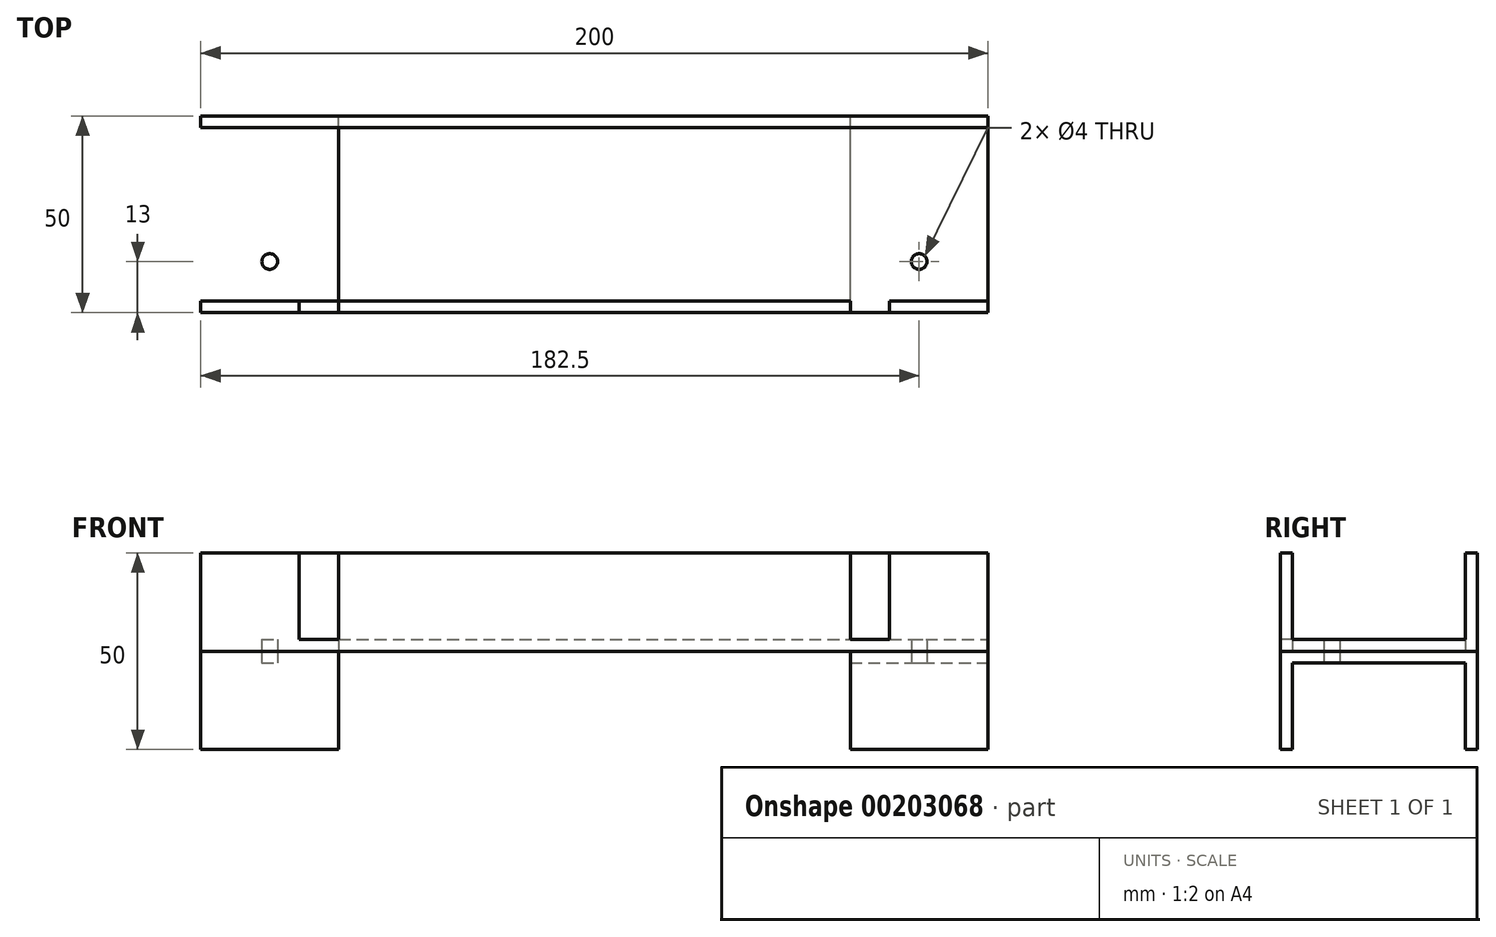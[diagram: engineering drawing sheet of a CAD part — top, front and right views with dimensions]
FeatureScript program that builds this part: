
annotation { "Feature Type Name" : "Feature", "Feature Type Description" : "" }
export const myFeature = defineFeature(function(context is Context, id is Id, definition is map)
    precondition{}
    {
        {
            var Q0;
            Q0=qCreatedBy(makeId("Front.planeOp"),FACE);
            var sketch = newSketch(context, id + "F0", { "sketchPlane" : qUnion([Q0])});
            skLineSegment(sketch, "E0.bottom", {"start": v(100, -12.5) * mm, "end": v(-100, -12.5) * mm});
            skLineSegment(sketch, "E0.top", {"start": v(100, 12.5) * mm, "end": v(-100, 12.5) * mm});
            skLineSegment(sketch, "E0.left", {"start": v(100, -12.5) * mm, "end": v(100, 12.5) * mm});
            skLineSegment(sketch, "E0.right", {"start": v(-100, -12.5) * mm, "end": v(-100, 12.5) * mm});
            skPoint(sketch, "E0.middle", {"position": v(0, 0) * mm});
            skSolve(sketch);
        }
        {
            var Q0;
            Q0 = qSketchRegion(id + "F0", true);
            extrude(context, id + "F1", {"entities" : qUnion([Q0]), "depth" : 50 * mm});
        }
        {
            var Q0;
            Q0=makeQuery(id+"F1.opExtrude","SWEPT_FACE",FACE,{"disambiguationData":[OSD([sQuery(id+"F0.wireOp",EDGE,"E0.left")])]});
            var sketch = newSketch(context, id + "F2", { "sketchPlane" : qUnion([Q0])});
            skLineSegment(sketch, "E1.bottom", {"start": v(-47, 12.5) * mm, "end": v(-3, 12.5) * mm});
            skLineSegment(sketch, "E1.top", {"start": v(-47, -9.5) * mm, "end": v(-3, -9.5) * mm});
            skLineSegment(sketch, "E1.left", {"start": v(-47, 12.5) * mm, "end": v(-47, -9.5) * mm});
            skLineSegment(sketch, "E1.right", {"start": v(-3, 12.5) * mm, "end": v(-3, -9.5) * mm});
            skLineSegment(sketch, "E2", {"start": v(-47, 4.4) * mm, "end": v(-50, 4.4) * mm});
            skLineSegment(sketch, "E3", {"start": v(-23.42, -9.5) * mm, "end": v(-23.42, -12.5) * mm});
            skLineSegment(sketch, "E4", {"start": v(-3, 6.89) * mm, "end": v(0, 6.89) * mm});
            skSolve(sketch);
        }
        {
            var Q0;
            {var subQ1=sQuery(id+"F2.wireOp",EDGE,"E1.bottom");Q0=makeQuery(id+"F2.imprint","IMPRINT",FACE,{"disambiguationData":[TD([[makeQuery(id+"F2.imprint","IMPRINT",EDGE,{"derivedFrom":subQ1}),-1.0]])]});}
            extrude(context, id + "F3", {"entities" : qUnion([Q0]), "operationType" : NewBodyOperationType.REMOVE, "endBound" : BoundingType.THROUGH_ALL, "oppositeDirection" : true, "depth" : 25 * mm});
        }
        {
            var Q0;
            Q0=makeQuery(id+"F1.opExtrude","CAP_FACE",FACE,{"disambiguationData":[OSD([sQuery(id+"F0.wireOp",EDGE,"E0.bottom"),sQuery(id+"F0.wireOp",EDGE,"E0.top"),sQuery(id+"F0.wireOp",EDGE,"E0.left"),sQuery(id+"F0.wireOp",EDGE,"E0.right")])],"isStart":false});
            var sketch = newSketch(context, id + "F4", { "sketchPlane" : qUnion([Q0])});
            skLineSegment(sketch, "E5.bottom", {"start": v(-75, 12.5) * mm, "end": v(-65, 12.5) * mm});
            skLineSegment(sketch, "E5.top", {"start": v(-75, -9.5) * mm, "end": v(-65, -9.5) * mm});
            skLineSegment(sketch, "E5.left", {"start": v(-75, 12.5) * mm, "end": v(-75, -9.5) * mm});
            skLineSegment(sketch, "E5.right", {"start": v(-65, 12.5) * mm, "end": v(-65, -9.5) * mm});
            skLineSegment(sketch, "E6.MirrorCS", {"start": v(65, 12.5) * mm, "end": v(65, -9.5) * mm});
            skLineSegment(sketch, "E7.MirrorCS", {"start": v(75, 12.5) * mm, "end": v(75, -9.5) * mm});
            skLineSegment(sketch, "E8.MirrorCS", {"start": v(75, 12.5) * mm, "end": v(65, 12.5) * mm});
            skLineSegment(sketch, "E9.MirrorCS", {"start": v(75, -9.5) * mm, "end": v(65, -9.5) * mm});
            skSolve(sketch);
        }
        {
            var Q0;
            Q0 = qSketchRegion(id + "F4", true);
            var Q1;
            Q1=makeQuery(id+"F3.boolean.opBoolean","COPY",FACE,{"derivedFrom":makeQuery(id+"F3.opExtrude","SWEPT_FACE",FACE,{"disambiguationData":[OSD([sQuery(id+"F2.wireOp",EDGE,"E1.right")])]})});
            extrude(context, id + "F5", {"entities" : qUnion([Q0]), "operationType" : NewBodyOperationType.REMOVE, "endBound" : BoundingType.UP_TO_SURFACE, "oppositeDirection" : true, "endBoundEntityFace" : qUnion([Q1]), "depth" : 25 * mm});
        }
        {
            var Q0;
            Q0=makeQuery(id+"F1.opExtrude","SWEPT_FACE",FACE,{"disambiguationData":[OSD([sQuery(id+"F0.wireOp",EDGE,"E0.bottom")])]});
            var sketch = newSketch(context, id + "F6", { "sketchPlane" : qUnion([Q0])});
            skLineSegment(sketch, "E10.bottom", {"start": v(-100, 50) * mm, "end": v(-65, 50) * mm});
            skLineSegment(sketch, "E10.top", {"start": v(-100, 0) * mm, "end": v(-65, 0) * mm});
            skLineSegment(sketch, "E10.left", {"start": v(-100, 50) * mm, "end": v(-100, 0) * mm});
            skLineSegment(sketch, "E10.right", {"start": v(-65, 50) * mm, "end": v(-65, 0) * mm});
            skSolve(sketch);
        }
        {
            var Q0;
            Q0 = qSketchRegion(id + "F6", true);
            extrude(context, id + "F7", {"entities" : qUnion([Q0]), "depth" : 25 * mm});
        }
        {
            var Q0;
            Q0=makeQuery(id+"F7.opExtrude","SWEPT_FACE",FACE,{"disambiguationData":[OSD([sQuery(id+"F6.wireOp",EDGE,"E10.left")])]});
            var sketch = newSketch(context, id + "F8", { "sketchPlane" : qUnion([Q0])});
            skLineSegment(sketch, "E11.bottom", {"start": v(3, -37.5) * mm, "end": v(47, -37.5) * mm});
            skLineSegment(sketch, "E11.top", {"start": v(3, -15.5) * mm, "end": v(47, -15.5) * mm});
            skLineSegment(sketch, "E11.left", {"start": v(3, -37.5) * mm, "end": v(3, -15.5) * mm});
            skLineSegment(sketch, "E11.right", {"start": v(47, -37.5) * mm, "end": v(47, -15.5) * mm});
            skLineSegment(sketch, "E12", {"start": v(3, -25.25) * mm, "end": v(0, -25.25) * mm});
            skPoint(sketch, "E12.endSnap0", {"position": v(0, -25) * mm});
            skLineSegment(sketch, "E13", {"start": v(22.26, -15.5) * mm, "end": v(22.26, -12.5) * mm});
            skLineSegment(sketch, "E14", {"start": v(47, -24.69) * mm, "end": v(50, -24.69) * mm});
            skSolve(sketch);
        }
        {
            var Q0;
            Q0 = qSketchRegion(id + "F8", true);
            extrude(context, id + "F9", {"entities" : qUnion([Q0]), "operationType" : NewBodyOperationType.REMOVE, "endBound" : BoundingType.THROUGH_ALL, "oppositeDirection" : true, "depth" : 25 * mm});
        }
        {
            var Q0;
            Q0=makeQuery(id+"F7.opExtrude","SWEPT_BODY",BODY,{"disambiguationData":[OSD([sQuery(id+"F6.wireOp",EDGE,"E10.bottom"),sQuery(id+"F6.wireOp",EDGE,"E10.top"),sQuery(id+"F6.wireOp",EDGE,"E10.left"),sQuery(id+"F6.wireOp",EDGE,"E10.right")])]});
            var Q1;
            Q1=qCreatedBy(makeId("Right.planeOp"),FACE);
            mirror(context, id + "F10", {"entities" : qUnion([Q0]), "mirrorPlane" : qUnion([Q1])});
        }
        {
            var Q0;
            Q0=makeQuery(id+"F9.boolean.opBoolean","COPY",FACE,{"derivedFrom":makeQuery(id+"F9.opExtrude","SWEPT_FACE",FACE,{"disambiguationData":[OSD([sQuery(id+"F8.wireOp",EDGE,"E11.top")])]})});
            var sketch = newSketch(context, id + "F11", { "sketchPlane" : qUnion([Q0])});
            skLineSegment(sketch, "E15", {"start": v(-82.5, 47) * mm, "end": v(-82.5, 3) * mm, "construction": true});
            skLineSegment(sketch, "E16", {"start": v(82.5, 3) * mm, "end": v(82.5, 47) * mm, "construction": true});
            skCircle(sketch, "E17", {"center": v(-82.5, 13) * mm, "radius": 2 * mm});
            skCircle(sketch, "E18.MirrorC", {"center": v(82.5, 13) * mm, "radius": 2 * mm});
            skLineSegment(sketch, "E19", {"start": v(-100, 25) * mm, "end": v(100, 25) * mm, "construction": true});
            skCircle(sketch, "E20.MirrorC", {"center": v(-82.5, 37) * mm, "radius": 2 * mm});
            skCircle(sketch, "E21.MirrorC", {"center": v(82.5, 37) * mm, "radius": 2 * mm});
            skSolve(sketch);
        }
        {
            var Q0;
            Q0=makeQuery(id+"F11.imprint","IMPRINT",FACE,{"disambiguationData":[TD([[makeQuery(id+"F11.imprint","IMPRINT",EDGE,{"derivedFrom":sQuery(id+"F11.wireOp",EDGE,"E20.MirrorC")}),-1.0]])]});
            var Q1;
            Q1=makeQuery(id+"F11.imprint","IMPRINT",FACE,{"disambiguationData":[TD([[makeQuery(id+"F11.imprint","IMPRINT",EDGE,{"derivedFrom":sQuery(id+"F11.wireOp",EDGE,"E17")}),1.0]])]});
            var Q2;
            Q2=makeQuery(id+"F11.imprint","IMPRINT",FACE,{"disambiguationData":[TD([[makeQuery(id+"F11.imprint","IMPRINT",EDGE,{"derivedFrom":sQuery(id+"F11.wireOp",EDGE,"E18.MirrorC")}),-1.0]])]});
            var Q3;
            Q3=makeQuery(id+"F11.imprint","IMPRINT",FACE,{"disambiguationData":[TD([[makeQuery(id+"F11.imprint","IMPRINT",EDGE,{"derivedFrom":sQuery(id+"F11.wireOp",EDGE,"E21.MirrorC")}),1.0]])]});
            extrude(context, id + "F12", {"entities" : qUnion([Q0, Q1, Q2, Q3]), "operationType" : NewBodyOperationType.REMOVE, "endBound" : BoundingType.THROUGH_ALL, "oppositeDirection" : true, "depth" : 25 * mm});
        }
    });
